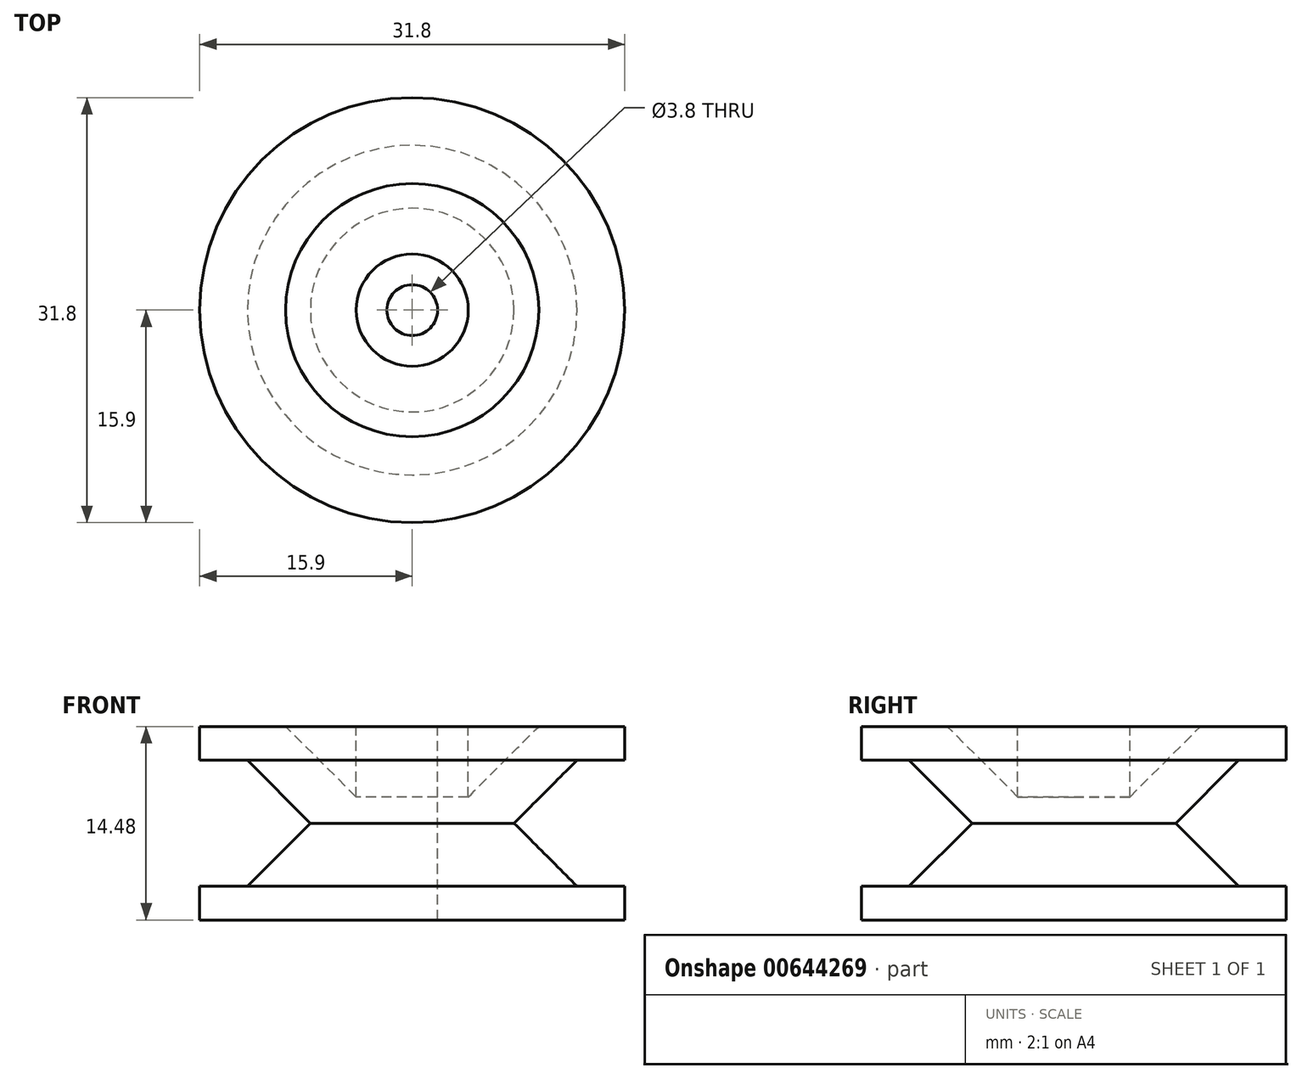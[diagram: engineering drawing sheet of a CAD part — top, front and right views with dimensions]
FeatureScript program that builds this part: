
annotation { "Feature Type Name" : "Feature", "Feature Type Description" : "" }
export const myFeature = defineFeature(function(context is Context, id is Id, definition is map)
    precondition{}
    {
        {
            var Q0;
            Q0=qCreatedBy(makeId("Top.planeOp"),FACE);
            var sketch = newSketch(context, id + "F0", { "sketchPlane" : qUnion([Q0])});
            skCircle(sketch, "E0", {"center": v(0, 0) * mm, "radius": 15.9 * mm});
            skSolve(sketch);
        }
        {
            var Q0;
            Q0 = qSketchRegion(id + "F0", true);
            extrude(context, id + "F1", {"entities" : qUnion([Q0]), "endBound" : BoundingType.SYMMETRIC, "depth" : 14.48 * mm, "offsetDistance" : 25.4 * mm});
        }
        {
            var Q0;
            Q0=makeQuery(id+"F1.opExtrude","CAP_FACE",FACE,{"disambiguationData":[OSD([sQuery(id+"F0.wireOp",EDGE,"E0")])],"isStart":false});
            var sketch = newSketch(context, id + "F2", { "sketchPlane" : qUnion([Q0])});
            skCircle(sketch, "E1", {"center": v(0, 0) * mm, "radius": 1.9 * mm});
            skSolve(sketch);
        }
        {
            var Q0;
            Q0=makeQuery(id+"F2.imprint","IMPRINT",FACE,{"disambiguationData":[TD([[makeQuery(id+"F2.imprint","IMPRINT",EDGE,{"derivedFrom":sQuery(id+"F2.wireOp",EDGE,"E1")}),1.0]])]});
            extrude(context, id + "F3", {"entities" : qUnion([Q0]), "operationType" : NewBodyOperationType.REMOVE, "endBound" : BoundingType.THROUGH_ALL, "oppositeDirection" : true, "depth" : 25.4 * mm, "offsetDistance" : 25.4 * mm});
        }
        {
            var Q0;
            Q0=qCreatedBy(makeId("Right.planeOp"),FACE);
            var sketch = newSketch(context, id + "F4", { "sketchPlane" : qUnion([Q0])});
            skLineSegment(sketch, "E2", {"start": v(20.4, 4.71) * mm, "end": v(12.33, 4.71) * mm});
            skLineSegment(sketch, "E3", {"start": v(12.33, 4.71) * mm, "end": v(7.62, 0) * mm});
            skLineSegment(sketch, "E4", {"start": v(7.62, 0) * mm, "end": v(12.33, -4.71) * mm});
            skLineSegment(sketch, "E5", {"start": v(12.33, -4.71) * mm, "end": v(20.4, -4.71) * mm});
            skLineSegment(sketch, "E6", {"start": v(20.4, -4.71) * mm, "end": v(20.4, 4.71) * mm});
            skLineSegment(sketch, "E7", {"start": v(0, 0) * mm, "end": v(0, 9.8) * mm, "construction": true});
            skLineSegment(sketch, "E8", {"start": v(4.2, 9.06) * mm, "end": v(4.2, 1.96) * mm});
            skLineSegment(sketch, "E9", {"start": v(4.2, 1.96) * mm, "end": v(11.3, 9.06) * mm});
            skLineSegment(sketch, "E10", {"start": v(11.3, 9.06) * mm, "end": v(4.2, 9.06) * mm});
            skSolve(sketch);
        }
        {
            var Q0;
            Q0 = qSketchRegion(id + "F4", true);
            var Q1;
            Q1=sQuery(id+"F4.wireOp",EDGE,"E7");
            revolve(context, id + "F5", {"operationType" : NewBodyOperationType.REMOVE, "entities" : qUnion([Q0]), "axis" : qUnion([Q1]), "revolveType" : RevolveType.FULL, "oppositeDirection" : true});
        }
    });
